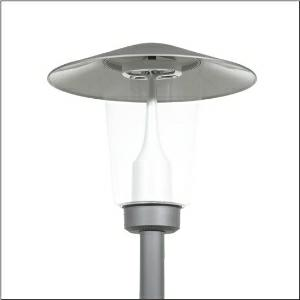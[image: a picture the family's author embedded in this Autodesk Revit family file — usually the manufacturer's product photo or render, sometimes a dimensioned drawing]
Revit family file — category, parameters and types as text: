
# Revit family: pilzleuchte_iq___st1_2a_5xa5235ef14hp_2efb
name_source: partatom
category: Lighting Fixtures
units: mm (PartAtom-declared; Revit-internal decimal feet)

## family parameters
Cut with Voids When Loaded = No
Host = Face
Light Source = No
Part Type = Normal
Room Calculation Point = No
Round Connector Dimension = Use Diameter
Shared = No

## types (1)
- --- (1 x LED, 4770 lm, 33.6 W, 3000K)
    Apparent Load = 34 VA
    CIE Flux Codes = 23 60 92 98 100
    Color Rendering = 70
    Color Temperature = 3000K
    Default Elevation = 1800 mm
    Description = Mushroom Luminaire iQ, mast luminaire, Module 540 iQ-SR, primary light control with 3 zone facetted reflector, of plastic, silver coated, highly specular, structured, primary optical cover: cover, of PMMA, transparent, light distribution: ST1.2a, light emission: direct distribution, primary light characteristic: asymmetric, installation type: post-top, LED, High Power LED, rated luminous flux: 4.770lm, luminous efficacy: 142lm/W, light colour: 730, colour temperature: 3000K, control gear: iQ Street-Remote, control: pre-setting: logarithmic dimming characteristic, Street-Remote, Auto-Match, Temp-Guard, Lumen-Switch, Night-Set, Smart-Wire, Light-Fading, Desk-Remote (wireless, voltage-free reading and setting of iQ features in the workshop via application-optimized NFC function/RFID function), optimised constant luminous flux control (CLO 2.0), with terminal, 6-pole, max. 2.5mm², mains connection: 230..240V, AC, 50/60Hz, start of lifetime: 34W, end of service life: 36W, reduction: 15W, luminaire housing, upper part, of glass-fibre reinforced polyester, coated, Siteco® metallic grey (DB 702S), diameter: 650mm, height: 586mm, spigot size: d x l = 76 x 70mm (post-top) | with reducer (optional accessory) 60 x 70mm, mounting height: 3..5m, post-top mast mounting element, of diecast aluminium, coated, Siteco® metallic grey (DB 702S), Module 540 iQ-SR, traffic white (RAL 9016), equipment: Power, protection rating (complete): IP65, insulation class (complete): insulation class II (safety insulation), certification: CE, ENEC, VDE, packaging unit: 1 piece

Light Distribution: ST1.2a
    Height = 586 mm
    Lamp = 1 x LED
    Lamp Light Flux = 4770 lm
    Lamp Power = 33.6 W
    Lamp count = 1
    Length = 650 mm
    Luminous efficacy = 142 lm/W
    Manufacturer = Siteco
    ModVariant = No
    Model = 5XA5235EF14HP
    Number of Poles = 1
    OnlyDefault = Yes
    Power Factor = 1
    Product Name = Pilzleuchte iQ | ST1.2a
    Product group = mast luminaire | pylon top
    ProductGroupID = 6100
    Protection Class = Protection class II
    Protection Degree = IP 65
    RLX_Detail_Level = 1
    RLX_Emergency_Light_Flux = 0 lm
    RLX_Emergency_Type = 0
    RLX_Emergency_Type_DB = No
    RlxData = <blob elided: 51653 chars, md5=b82a39e0>
    Socket = socket
    Standby Power = 0 W
    System Light Flux = 4770 lm
    System Power = 34 W
    Type Comments = factory setting: luminous flux: 100 % | dim-lin: 254 | 695 mA
    Type Image = l_1006077.jpg
    URL = http://relux.com
    VarID = @adj_193620
    Voltage = 0 V
    Weight = 0.00 kg
    Width = 0 mm  [stored 0 ft]

note: [stored X ft] marks values corroborated as IEEE doubles in the binary element streams (Revit-internal decimal feet)

## geometry (parser evidence)
native form markers: Blend x4, Sweep x12
no freeform markers — native parametric forms only
